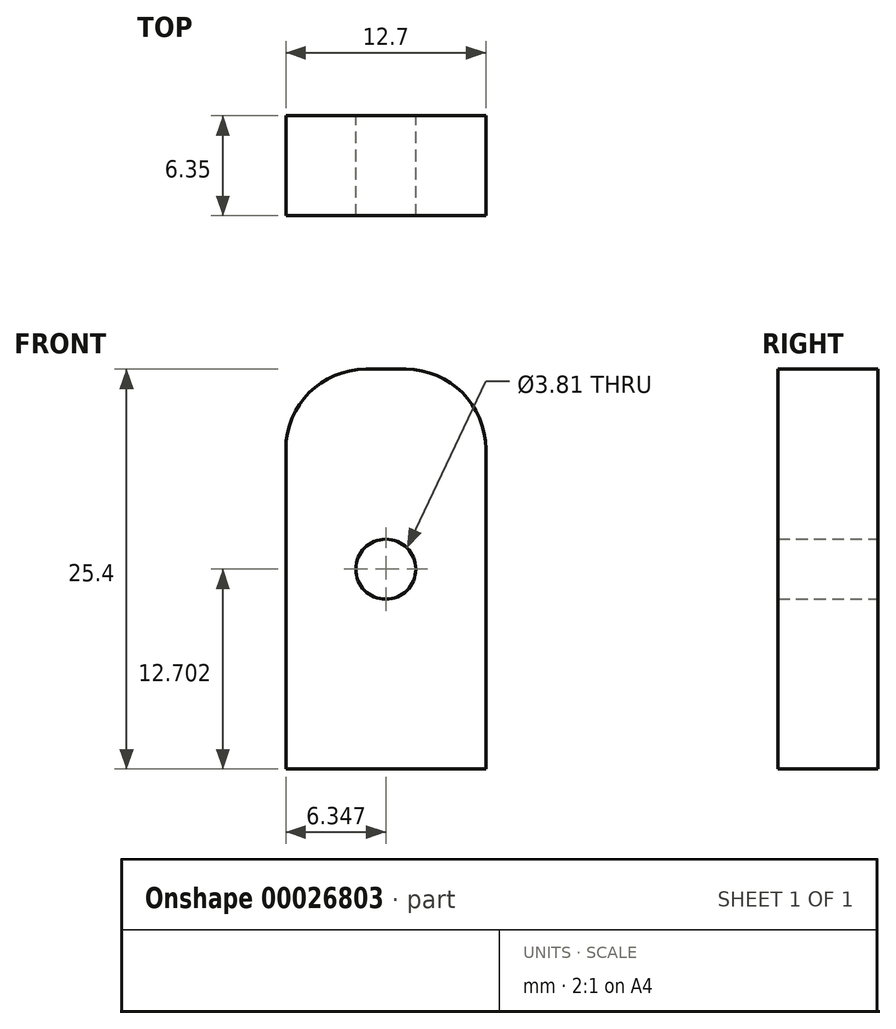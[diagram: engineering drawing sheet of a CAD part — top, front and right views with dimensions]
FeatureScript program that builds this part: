
annotation { "Feature Type Name" : "Feature", "Feature Type Description" : "" }
export const myFeature = defineFeature(function(context is Context, id is Id, definition is map)
    precondition{}
    {
        {
            var Q0;
            Q0=qCreatedBy(makeId("Front.planeOp"),FACE);
            var sketch = newSketch(context, id + "F0", { "sketchPlane" : qUnion([Q0])});
            skLineSegment(sketch, "E0.bottom", {"start": v(-58.34, 23.97) * mm, "end": v(-45.64, 23.97) * mm});
            skLineSegment(sketch, "E0.top", {"start": v(-58.34, -1.43) * mm, "end": v(-45.64, -1.43) * mm});
            skLineSegment(sketch, "E0.left", {"start": v(-58.34, 23.97) * mm, "end": v(-58.34, -1.43) * mm});
            skLineSegment(sketch, "E0.right", {"start": v(-45.64, 23.97) * mm, "end": v(-45.64, -1.43) * mm});
            skPoint(sketch, "E1.orphan", {"position": v(-52, -1.43) * mm});
            skPoint(sketch, "E2.start.orphan", {"position": v(-52, 23.97) * mm});
            skLineSegment(sketch, "E3", {"start": v(-52, 23.97) * mm, "end": v(-52, -1.43) * mm});
            skCircle(sketch, "E4", {"center": v(-52, 11.27) * mm, "radius": 1.9 * mm});
            skSolve(sketch);
        }
        {
            var Q0;
            Q0=makeQuery(id+"F0.imprint","IMPRINT",FACE,{"disambiguationData":[TD([[makeQuery(id+"F0.imprint","IMPRINT",EDGE,{"derivedFrom":sQuery(id+"F0.wireOp",EDGE,"E0.bottom")}),-1.0]])]});
            extrude(context, id + "F1", {"entities" : qUnion([Q0]), "depth" : 6.35 * mm});
        }
        {
            var Q0;
            Q0=makeQuery(id+"F1.opExtrude","SWEPT_EDGE",EDGE,{"disambiguationData":[OSD([sQuery(id+"F0.wireOp",EDGE,"E0.bottom"),sQuery(id+"F0.wireOp",EDGE,"E0.right")])]});
            fillet(context, id + "F2", {"entities" : qUnion([Q0]), "radius" : 5.08 * mm, "tangentPropagation" : true, "allowEdgeOverflow" : false});
        }
        {
            var Q0;
            Q0=makeQuery(id+"F1.opExtrude","SWEPT_EDGE",EDGE,{"disambiguationData":[OSD([sQuery(id+"F0.wireOp",EDGE,"E0.bottom"),sQuery(id+"F0.wireOp",EDGE,"E0.left")])]});
            fillet(context, id + "F3", {"entities" : qUnion([Q0]), "radius" : 5.08 * mm, "tangentPropagation" : true, "allowEdgeOverflow" : false});
        }
    });
